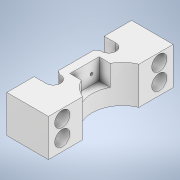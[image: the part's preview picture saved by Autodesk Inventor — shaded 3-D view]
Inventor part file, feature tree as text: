
AUTODESK INVENTOR PART (.ipt)
format: ipt  version: 2020 (Build 240168000, 168)  size: 211,456 bytes
history: native  units: mm
features: extrude x6, sketch x5, other x1
ambient origin geometry x8: Origin, YZ Plane, XZ Plane, XY Plane, X Axis, Y Axis, Z Axis, Center Point
bodies: Body1 (feature_tree)
feature tree (12):
  other  "Bryła1"
  extrude  "Wyciągnięcie proste1"  Depth=1.0mm
  sketch  "Szkic3"
  extrude  "Wyciągnięcie proste2"  Depth=20.0mm
  extrude  "Wyciągnięcie proste3"  Depth=90.0mm
  extrude  "Wyciągnięcie proste4"  Depth=45.0mm
  extrude  "Wyciągnięcie proste8"  Depth=30.0mm
  extrude  "Wyciągnięcie proste9"  Depth=27.0mm TaperAngle=0.0deg
  sketch  "Szkic2"
  sketch  "Szkic4"
  sketch  "Szkic8"
  sketch  "Szkic9"
